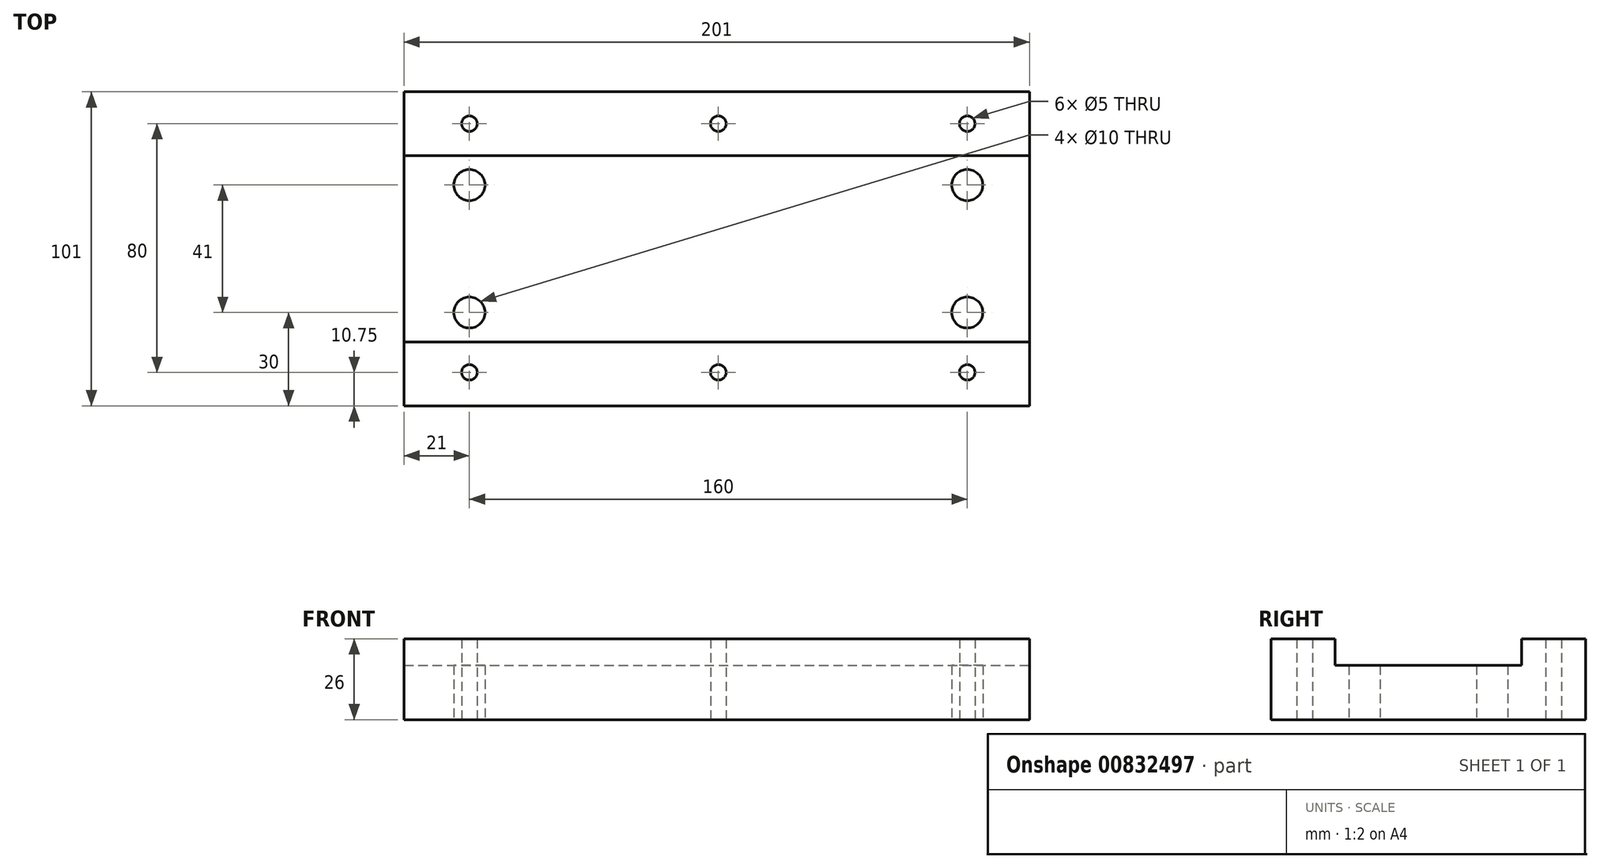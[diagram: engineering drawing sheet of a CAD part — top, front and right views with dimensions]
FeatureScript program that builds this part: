
annotation { "Feature Type Name" : "Feature", "Feature Type Description" : "" }
export const myFeature = defineFeature(function(context is Context, id is Id, definition is map)
    precondition{}
    {
        {
            var Q0;
            Q0=qCreatedBy(makeId("Top.planeOp"),FACE);
            var sketch = newSketch(context, id + "F0", { "sketchPlane" : qUnion([Q0])});
            skLineSegment(sketch, "E0.bottom", {"start": v(-100.5, 50.5) * mm, "end": v(100.5, 50.5) * mm});
            skLineSegment(sketch, "E0.top", {"start": v(-100.5, -50.5) * mm, "end": v(100.5, -50.5) * mm});
            skLineSegment(sketch, "E0.left", {"start": v(-100.5, 50.5) * mm, "end": v(-100.5, -50.5) * mm});
            skLineSegment(sketch, "E0.right", {"start": v(100.5, 50.5) * mm, "end": v(100.5, -50.5) * mm});
            skLineSegment(sketch, "E1.bottom", {"start": v(-100.5, 30) * mm, "end": v(100.5, 30) * mm});
            skLineSegment(sketch, "E1.top", {"start": v(-100.5, -30) * mm, "end": v(100.5, -30) * mm});
            skLineSegment(sketch, "E1.left", {"start": v(-100.5, 30) * mm, "end": v(-100.5, -30) * mm});
            skLineSegment(sketch, "E1.right", {"start": v(100.5, 30) * mm, "end": v(100.5, -30) * mm});
            skCircle(sketch, "E2", {"center": v(-79.5, 40.25) * mm, "radius": 2.5 * mm});
            skCircle(sketch, "E3", {"center": v(-79.5, 20.5) * mm, "radius": 5 * mm});
            skCircle(sketch, "E4.0.1.0", {"center": v(-79.5, -39.75) * mm, "radius": 2.5 * mm});
            skCircle(sketch, "E4.1.0.0", {"center": v(0.5, 40.25) * mm, "radius": 2.5 * mm});
            skCircle(sketch, "E4.1.1.0", {"center": v(0.5, -39.75) * mm, "radius": 2.5 * mm});
            skCircle(sketch, "E4.2.0.0", {"center": v(80.5, 40.25) * mm, "radius": 2.5 * mm});
            skCircle(sketch, "E4.2.1.0", {"center": v(80.5, -39.75) * mm, "radius": 2.5 * mm});
            skLineSegment(sketch, "E4.direction1", {"start": v(-79.5, 40.25) * mm, "end": v(0.5, 40.25) * mm, "construction": true});
            skLineSegment(sketch, "E4.direction2", {"start": v(-79.5, 40.25) * mm, "end": v(-79.5, -39.75) * mm, "construction": true});
            skCircle(sketch, "E5.0.1.0", {"center": v(-79.5, -20.5) * mm, "radius": 5 * mm});
            skCircle(sketch, "E5.1.0.0", {"center": v(80.5, 20.5) * mm, "radius": 5 * mm});
            skCircle(sketch, "E5.1.1.0", {"center": v(80.5, -20.5) * mm, "radius": 5 * mm});
            skCircle(sketch, "E5.2.0.0", {"center": v(240.5, 20.5) * mm, "radius": 5 * mm});
            skCircle(sketch, "E5.2.1.0", {"center": v(240.5, -20.5) * mm, "radius": 5 * mm});
            skLineSegment(sketch, "E5.direction1", {"start": v(-79.5, 20.5) * mm, "end": v(80.5, 20.5) * mm, "construction": true});
            skLineSegment(sketch, "E5.direction2", {"start": v(-79.5, 20.5) * mm, "end": v(-79.5, -20.5) * mm, "construction": true});
            skSolve(sketch);
        }
        {
            var Q0;
            {var subQ2=sQuery(id+"F0.wireOp",EDGE,"E0.bottom");Q0=makeQuery(id+"F0.imprint","IMPRINT",FACE,{"disambiguationData":[TD([[makeQuery(id+"F0.imprint","IMPRINT",EDGE,{"derivedFrom":subQ2}),-1.0]])]});}
            var Q1;
            {var subQ2=sQuery(id+"F0.wireOp",EDGE,"E0.top");Q1=makeQuery(id+"F0.imprint","IMPRINT",FACE,{"disambiguationData":[TD([[makeQuery(id+"F0.imprint","IMPRINT",EDGE,{"derivedFrom":subQ2}),1.0]])]});}
            extrude(context, id + "F1", {"entities" : qUnion([Q0, Q1]), "depth" : 26 * mm, "offsetDistance" : 25 * mm});
        }
        {
            var Q0;
            Q0=makeQuery(id+"F0.imprint","IMPRINT",FACE,{"disambiguationData":[TD([[makeQuery(id+"F0.imprint","IMPRINT",EDGE,{"derivedFrom":sQuery(id+"F0.wireOp",EDGE,"E1.bottom")}),-1.0]])]});
            extrude(context, id + "F2", {"entities" : qUnion([Q0]), "operationType" : NewBodyOperationType.ADD, "depth" : 17.5 * mm, "offsetDistance" : 25 * mm});
        }
    });
